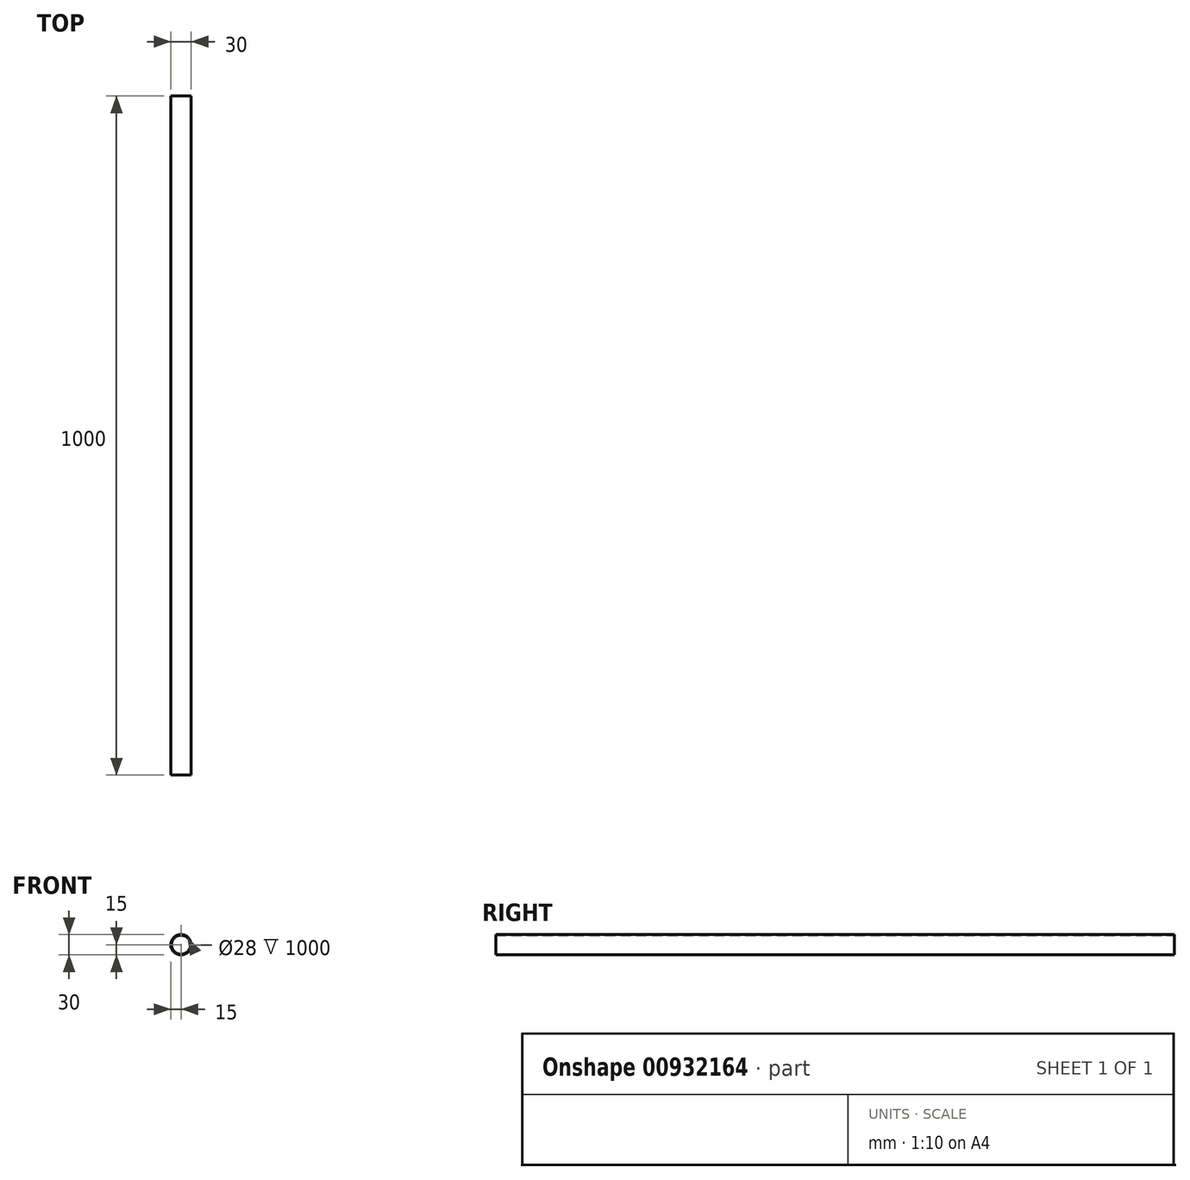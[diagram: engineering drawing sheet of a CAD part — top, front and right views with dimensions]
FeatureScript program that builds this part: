
annotation { "Feature Type Name" : "Feature", "Feature Type Description" : "" }
export const myFeature = defineFeature(function(context is Context, id is Id, definition is map)
    precondition{}
    {
        {
            var Q0;
            Q0=qCreatedBy(makeId("Front.planeOp"),FACE);
            var sketch = newSketch(context, id + "F0", { "sketchPlane" : qUnion([Q0])});
            skCircle(sketch, "E0", {"center": v(0, 0) * mm, "radius": 14 * mm});
            skCircle(sketch, "E1", {"center": v(0, 0) * mm, "radius": 15 * mm});
            skSolve(sketch);
        }
        {
            var Q0;
            Q0=makeQuery(id+"F0.imprint","IMPRINT",FACE,{"disambiguationData":[TD([[makeQuery(id+"F0.imprint","IMPRINT",EDGE,{"derivedFrom":sQuery(id+"F0.wireOp",EDGE,"E0")}),-1.0]])]});
            extrude(context, id + "F1", {"entities" : qUnion([Q0]), "depth" : 1000 * mm, "offsetDistance" : 25 * mm});
        }
    });
